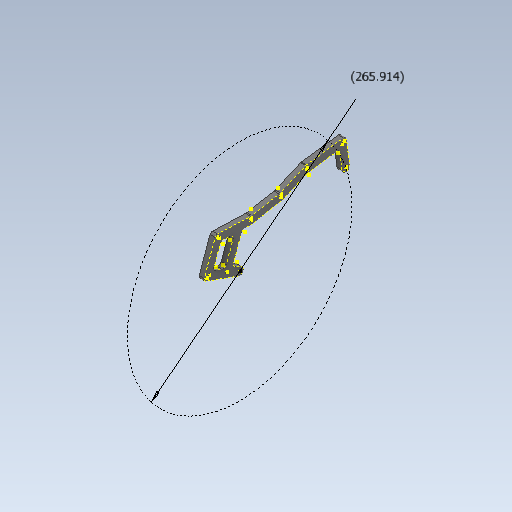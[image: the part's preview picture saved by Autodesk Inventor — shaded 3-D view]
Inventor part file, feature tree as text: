
AUTODESK INVENTOR PART (.ipt)
format: ipt  version: 2020 (Build 240168000, 168)  size: 306,176 bytes
history: native  units: in
note: dims shown in document units (in); Inventor stores cm internally (conversion verified against a paired STEP export)
features: sketch x4, projected_geometry x3, extrude x1
ambient origin geometry x8: Origin, YZ Plane, XZ Plane, XY Plane, X Axis, Y Axis, Z Axis, Center Point
bodies: Solid2 (feature_tree), Solid1 (feature_tree)
feature tree (8):
  extrude  "Extrusion1"  Depth=0.0787in
  sketch  "Sketch3"  dims[d3=0.122in]
  sketch  "Sketch4"  dims[d4=0.122in]
  sketch  "Sketch5"  dims[d5=0.122in d6=0.122in d7=0.122in d8=0.122in d9=0.122in d10=0.122in d11=10.4691in]
  sketch  "Sketch1"  dims[d0=0.0787in d1=0.0in d2=0.122in]
  projected_geometry  "Projected Loop1"
  projected_geometry  "Projected Loop2"
  projected_geometry  "Projected Loop3"
